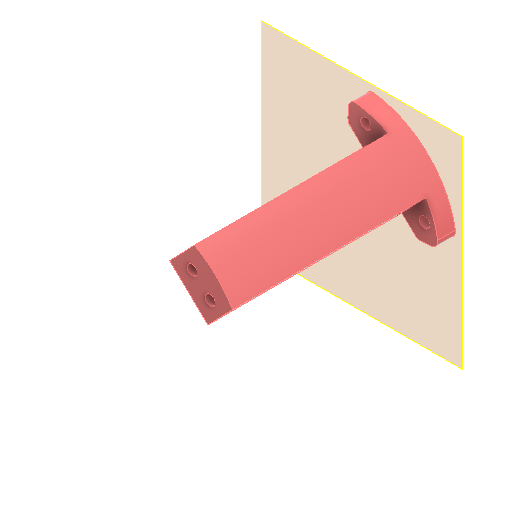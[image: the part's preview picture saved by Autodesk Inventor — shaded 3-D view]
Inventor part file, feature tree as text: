
AUTODESK INVENTOR PART (.ipt)
format: ipt  version: 2022 (Build 260153000, 153)  size: 166,400 bytes
history: native  units: mm
features: extrude x3, sketch x2, projected_geometry x2, other x2, plane x1, fillet x1, reference x1
ambient origin geometry x8: Origin, YZ Plane, XZ Plane, XY Plane, X Axis, Y Axis, Z Axis, Center Point
bodies: Volumenkörper1 (feature_tree)
feature tree (12):
  plane  "Arbeitsebene1"
  extrude  "Extrusion1"  Depth=5.0mm
  fillet  "Rundung1"  Radius=5.0mm
  extrude  "Extrusion2"  Depth=20.0mm
  extrude  "Extrusion3"  Depth=20.0mm
  reference  "Referenz1"
  sketch  "Skizze2"  dims[d1=6.0mm d2=5.0mm d3=5.0mm]
  projected_geometry  "Projizierte Kontur1"
  sketch  "Skizze3"  dims[d4=5.0mm d5=0.0mm d6=3.0mm d7=3.0mm d8=2.0mm d9=4.0mm d10=4.0mm d11=55.0mm d12=0.0mm d13=2.8mm d14=2.8mm d15=4.0mm d16=4.0mm d17=5.0mm d18=5.0mm d19=20.0mm d20=0.0mm]
  projected_geometry  "Projizierte Kontur2"
  other  "Assembly_Matchboxscope_injectionmolded_holo.iam"
  other  "IM_Matchboxscope_base:1"
